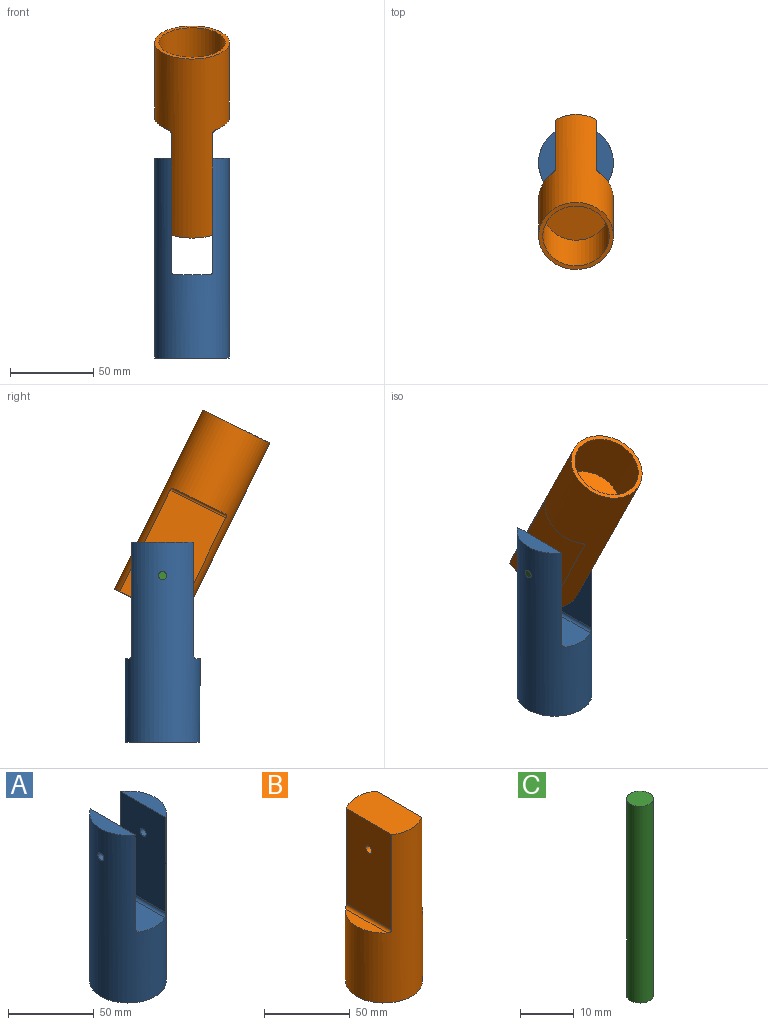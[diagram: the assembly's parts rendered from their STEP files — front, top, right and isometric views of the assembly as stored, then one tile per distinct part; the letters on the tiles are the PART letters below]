
ASSEMBLY  parts=3 mates=2
PART A: 13 faces, bbox 45x45x120 mm
  f0: cylinder r=22.5mm len=120mm, axis (0,0,-1), area 13218.5mm2, adj f1,f2,f3,f4,f5,f6,f9,f10
  f1: plane 37.42x10mm, normal (0,0,1), area 263.2mm2, adj f0,f5
  f2: plane 37.42x10mm, normal (0,0,1), area 263.2mm2, adj f0,f4
  f3: plane 45x45mm, normal (0,0,-1), area 333.8mm2, adj f0,f7
  f4: plane 68x37.42mm, normal (1,0,0), area 2524.7mm2, adj f0,f2,f10,f11
  f5: plane 68x37.42mm, normal (-1,0,0), area 2524.7mm2, adj f0,f1,f9,f12
  f6: plane 45x21mm, normal (0,0,1), area 909.5mm2, adj f0,f11,f12
  f7: cylinder r=20mm len=40mm, axis (0,0,-1), area 4398.2mm2, adj f3,f8
  f8: plane 40x40mm, normal (0,0,-1), area 1256.6mm2, adj f7
  f9: cylinder r=2.5mm len=10mm, axis (1,0,0), area 156mm2, adj f0,f5
  f10: cylinder r=2.5mm len=10mm, axis (1,0,0), area 156mm2, adj f0,f4
  f11: cylinder r=2mm len=39.8mm, axis (0,-1,0), area 120.4mm2, adj f0,f4,f6
  f12: cylinder r=2mm len=39.8mm, axis (0,1,0), area 120.4mm2, adj f0,f5,f6
PART B: 12 faces, bbox 45x45x120 mm
  f0: plane 45x25mm, normal (0,0,1), area 1064.1mm2, adj f1,f3,f5
  f1: cylinder r=22.5mm len=120mm, axis (0,0,-1), area 10783.7mm2, adj f0,f2,f3,f4,f5,f6,f10,f11
  f2: plane 45x45mm, normal (0,0,-1), area 333.8mm2, adj f1,f7
  f3: plane 68x37.42mm, normal (-1,0,0), area 2524.7mm2, adj f0,f1,f9,f10
  f4: plane 34.41x8mm, normal (0,0,1), area 191.2mm2, adj f1,f10
  f5: plane 68x37.42mm, normal (1,0,0), area 2524.7mm2, adj f0,f1,f9,f11
  f6: plane 34.41x8mm, normal (0,0,1), area 191.2mm2, adj f1,f11
  f7: cylinder r=20mm len=40mm, axis (0,0,-1), area 4398.2mm2, adj f2,f8
  f8: plane 40x40mm, normal (0,0,-1), area 1256.6mm2, adj f7
  f9: cylinder r=2.5mm len=25mm, axis (1,0,0), area 392.7mm2, adj f3,f5
  f10: cylinder r=2mm len=37.42mm, axis (0,1,0), area 114.3mm2, adj f1,f3,f4
  f11: cylinder r=2mm len=37.42mm, axis (0,-1,0), area 114.3mm2, adj f1,f5,f6
PART C: 3 faces, bbox 5x5x45 mm
  f0: cylinder r=2.5mm len=45mm, axis (0,0,-1), area 706.9mm2, adj f1,f2
  f1: plane 5x5mm, normal (0,0,1), area 19.6mm2, adj f0
  f2: plane 5x5mm, normal (0,0,-1), area 19.6mm2, adj f0
PLACE A t=(-102.01,-28.5,-14.4)mm fixed
PLACE B rot(axis=(-1,0,0),153.8deg) t=(-101.95,-72.69,175.3)mm
PLACE C rot(axis=(0.71,0,0.71),180deg) t=(-124.45,-28.5,85.6)mm
MATE fastened A.f9 <-> C.f0  axis (1,0,0) through (-79.45,-28.5,85.6)mm
MATE revolute C.f0 <-> B.f9  axis (-1,0,0) through (-101.95,-28.5,85.6)mm
